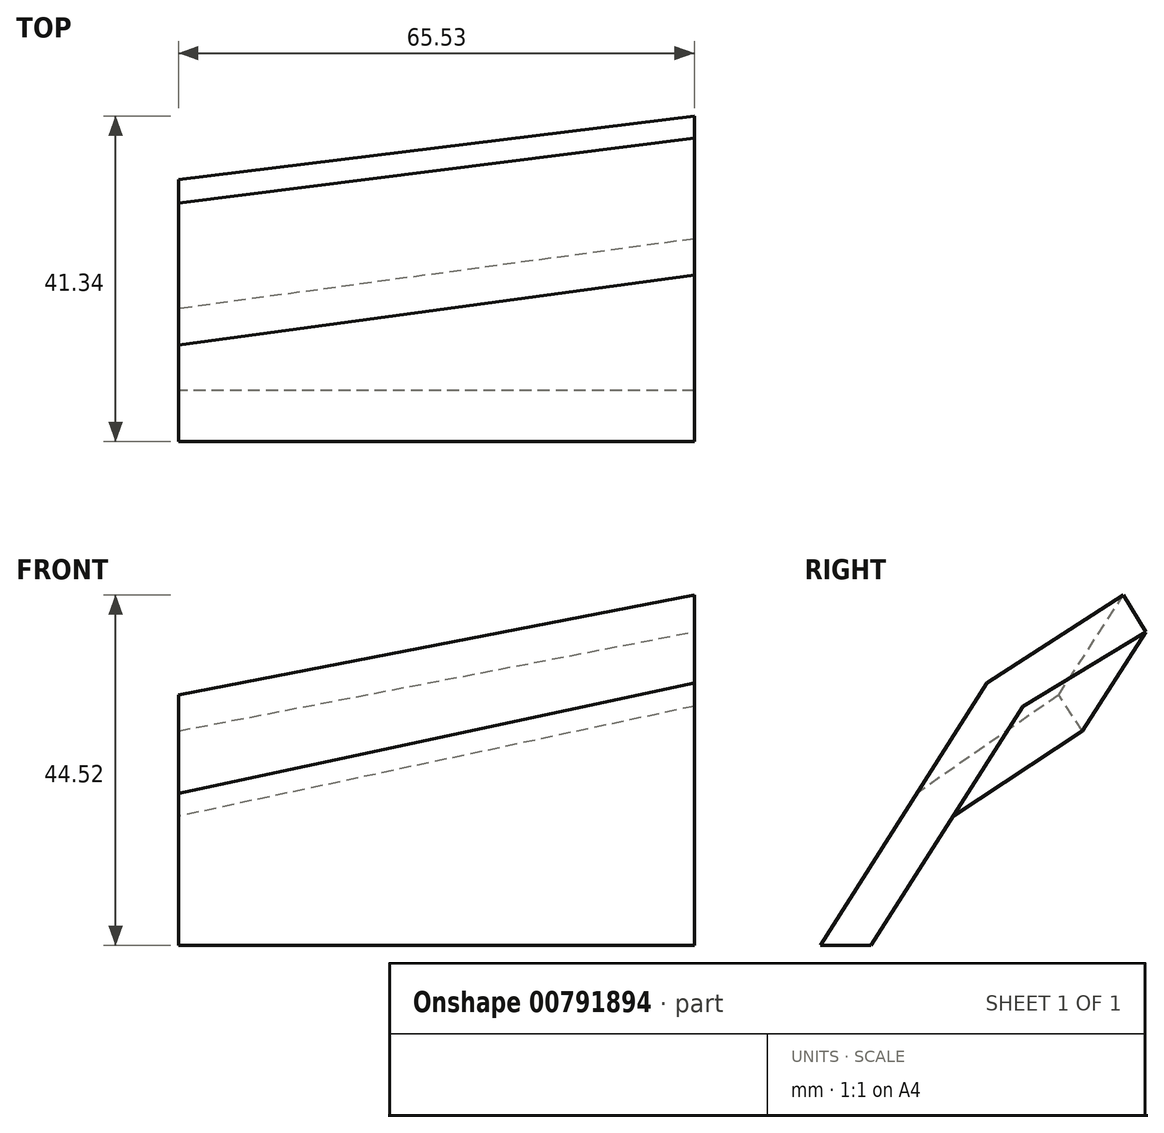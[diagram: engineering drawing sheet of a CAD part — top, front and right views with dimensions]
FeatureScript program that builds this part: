
annotation { "Feature Type Name" : "Feature", "Feature Type Description" : "" }
export const myFeature = defineFeature(function(context is Context, id is Id, definition is map)
    precondition{}
    {
        {
            var Q0;
            Q0=qCreatedBy(makeId("Right.planeOp"),FACE);
            var sketch = newSketch(context, id + "F0", { "sketchPlane" : qUnion([Q0])});
            skLineSegment(sketch, "E0", {"start": v(-24.93, 0) * mm, "end": v(9.93, 54.95) * mm});
            skLineSegment(sketch, "E1", {"start": v(9.93, 54.95) * mm, "end": v(14.54, 52.03) * mm});
            skLineSegment(sketch, "E2", {"start": v(14.54, 52.03) * mm, "end": v(-18.47, 0) * mm});
            skLineSegment(sketch, "E3", {"start": v(-18.47, 0) * mm, "end": v(-24.93, 0) * mm});
            skSolve(sketch);
        }
        {
            var Q0;
            Q0 = qSketchRegion(id + "F0", true);
            extrude(context, id + "F1", {"entities" : qUnion([Q0]), "depth" : 65.53 * mm, "offsetDistance" : 25.4 * mm});
        }
        {
            var Q0;
            Q0=makeQuery(id+"F1.opExtrude","SWEPT_FACE",FACE,{"disambiguationData":[OSD([sQuery(id+"F0.wireOp",EDGE,"E0")])]});
            var sketch = newSketch(context, id + "F2", { "sketchPlane" : qUnion([Q0])});
            skLineSegment(sketch, "E4", {"start": v(0, 9.54) * mm, "end": v(65.53, 26.1) * mm});
            skLineSegment(sketch, "E5", {"start": v(65.53, 26.1) * mm, "end": v(82.35, 60.76) * mm});
            skLineSegment(sketch, "E6", {"start": v(82.35, 60.76) * mm, "end": v(0, 74.2) * mm});
            skLineSegment(sketch, "E7", {"start": v(0, 74.2) * mm, "end": v(-17.96, 38.16) * mm});
            skLineSegment(sketch, "E8", {"start": v(-17.96, 38.16) * mm, "end": v(0, 9.54) * mm});
            skSolve(sketch);
        }
        {
            var Q0;
            Q0 = qSketchRegion(id + "F2", true);
            extrude(context, id + "F3", {"entities" : qUnion([Q0]), "operationType" : NewBodyOperationType.REMOVE, "oppositeDirection" : true, "depth" : 25.4 * mm, "offsetDistance" : 25.4 * mm});
        }
        {
            var Q0;
            Q0=makeQuery(id+"F1.opExtrude","CAP_FACE",FACE,{"disambiguationData":[OSD([sQuery(id+"F0.wireOp",EDGE,"E0"),sQuery(id+"F0.wireOp",EDGE,"E1"),sQuery(id+"F0.wireOp",EDGE,"E2"),sQuery(id+"F0.wireOp",EDGE,"E3")])],"isStart":false});
            var sketch = newSketch(context, id + "F4", { "sketchPlane" : qUnion([Q0])});
            skLineSegment(sketch, "E9", {"start": v(0.81, 30.4) * mm, "end": v(16.41, 39.85) * mm});
            skLineSegment(sketch, "E10", {"start": v(16.41, 39.85) * mm, "end": v(13.58, 44.52) * mm});
            skLineSegment(sketch, "E11", {"start": v(13.58, 44.52) * mm, "end": v(-3.8, 33.32) * mm});
            skLineSegment(sketch, "E12", {"start": v(-3.8, 33.32) * mm, "end": v(0.81, 30.4) * mm});
            skSolve(sketch);
        }
        {
            var Q0;
            Q0=makeQuery(id+"F1.opExtrude","CAP_FACE",FACE,{"disambiguationData":[OSD([sQuery(id+"F0.wireOp",EDGE,"E0"),sQuery(id+"F0.wireOp",EDGE,"E1"),sQuery(id+"F0.wireOp",EDGE,"E2"),sQuery(id+"F0.wireOp",EDGE,"E3")])],"isStart":true});
            var sketch = newSketch(context, id + "F5", { "sketchPlane" : qUnion([Q0])});
            skLineSegment(sketch, "E13", {"start": v(8.06, 16.4) * mm, "end": v(-8.36, 27.25) * mm});
            skLineSegment(sketch, "E14", {"start": v(-8.36, 27.25) * mm, "end": v(-5.35, 31.81) * mm});
            skLineSegment(sketch, "E15", {"start": v(-5.35, 31.81) * mm, "end": v(12.67, 19.33) * mm});
            skLineSegment(sketch, "E16", {"start": v(12.67, 19.33) * mm, "end": v(8.06, 16.4) * mm});
            skSolve(sketch);
        }
        {
            var Q1;
            Q1=makeQuery(id+"F5.imprint","IMPRINT",FACE,{"disambiguationData":[TD([[makeQuery(id+"F5.imprint","IMPRINT",EDGE,{"derivedFrom":sQuery(id+"F5.wireOp",EDGE,"E13")}),-1.0]])]});
            var Q2;
            Q2=makeQuery(id+"F4.imprint","IMPRINT",FACE,{"disambiguationData":[TD([[makeQuery(id+"F4.imprint","IMPRINT",EDGE,{"derivedFrom":sQuery(id+"F4.wireOp",EDGE,"E9")}),1.0]])]});
            loft(context, id + "F6", {"operationType" : NewBodyOperationType.ADD, "sheetProfilesArray" : [{ "sheetProfileEntities" : qUnion([Q1]) }, { "sheetProfileEntities" : qUnion([Q2]) }]});
        }
    });
